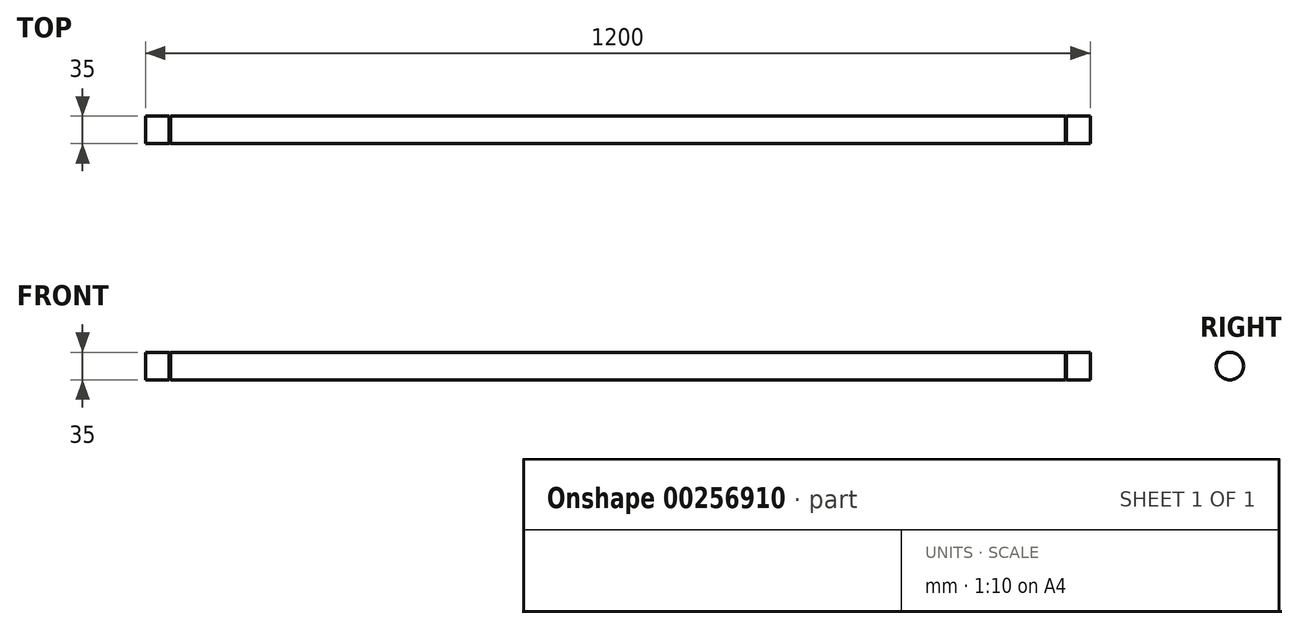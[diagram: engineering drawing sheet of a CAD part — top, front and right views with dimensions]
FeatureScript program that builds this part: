
annotation { "Feature Type Name" : "Feature", "Feature Type Description" : "" }
export const myFeature = defineFeature(function(context is Context, id is Id, definition is map)
    precondition{}
    {
        {
            var Q0;
            Q0=qCreatedBy(makeId("Right.planeOp"),FACE);
            var sketch = newSketch(context, id + "F0", { "sketchPlane" : qUnion([Q0])});
            skCircle(sketch, "E0", {"center": v(0, 0) * mm, "radius": 17.5 * mm});
            skSolve(sketch);
        }
        {
            var Q0;
            Q0=makeQuery(id+"F0.imprint","IMPRINT",FACE,{"disambiguationData":[TD([[makeQuery(id+"F0.imprint","IMPRINT",EDGE,{"derivedFrom":sQuery(id+"F0.wireOp",EDGE,"E0")}),1.0]])]});
            extrude(context, id + "F1", {"entities" : qUnion([Q0]), "oppositeDirection" : true, "depth" : 1200 * mm});
        }
        {
            var Q0;
            Q0=qCreatedBy(makeId("Front.planeOp"),FACE);
            var sketch = newSketch(context, id + "F2", { "sketchPlane" : qUnion([Q0])});
            skLineSegment(sketch, "E1", {"start": v(0, 0) * mm, "end": v(-1200, 0) * mm, "construction": true});
            skLineSegment(sketch, "E2.bottom", {"start": v(-30, 17.5) * mm, "end": v(-31.6, 17.5) * mm});
            skLineSegment(sketch, "E2.top", {"start": v(-30, 16.5) * mm, "end": v(-31.6, 16.5) * mm});
            skLineSegment(sketch, "E2.left", {"start": v(-30, 17.5) * mm, "end": v(-30, 16.5) * mm});
            skLineSegment(sketch, "E2.right", {"start": v(-31.6, 17.5) * mm, "end": v(-31.6, 16.5) * mm});
            skPoint(sketch, "E3", {"position": v(-600, 0) * mm});
            skLineSegment(sketch, "E4", {"start": v(-600, 0) * mm, "end": v(-600, 96.3) * mm, "construction": true});
            skLineSegment(sketch, "E5.MirrorCS", {"start": v(-1168.4, 17.5) * mm, "end": v(-1168.4, 16.5) * mm});
            skLineSegment(sketch, "E6.MirrorCS", {"start": v(-1170, 17.5) * mm, "end": v(-1170, 16.5) * mm});
            skLineSegment(sketch, "E7.MirrorCS", {"start": v(-1170, 16.5) * mm, "end": v(-1168.4, 16.5) * mm});
            skLineSegment(sketch, "E8.MirrorCS", {"start": v(-1170, 17.5) * mm, "end": v(-1168.4, 17.5) * mm});
            skSolve(sketch);
        }
        {
            var Q0;
            Q0 = qSketchRegion(id + "F2", true);
            var Q1;
            Q1=sQuery(id+"F2.wireOp",EDGE,"E1");
            revolve(context, id + "F3", {"operationType" : NewBodyOperationType.REMOVE, "entities" : qUnion([Q0]), "axis" : qUnion([Q1]), "revolveType" : RevolveType.FULL, "oppositeDirection" : true});
        }
    });
